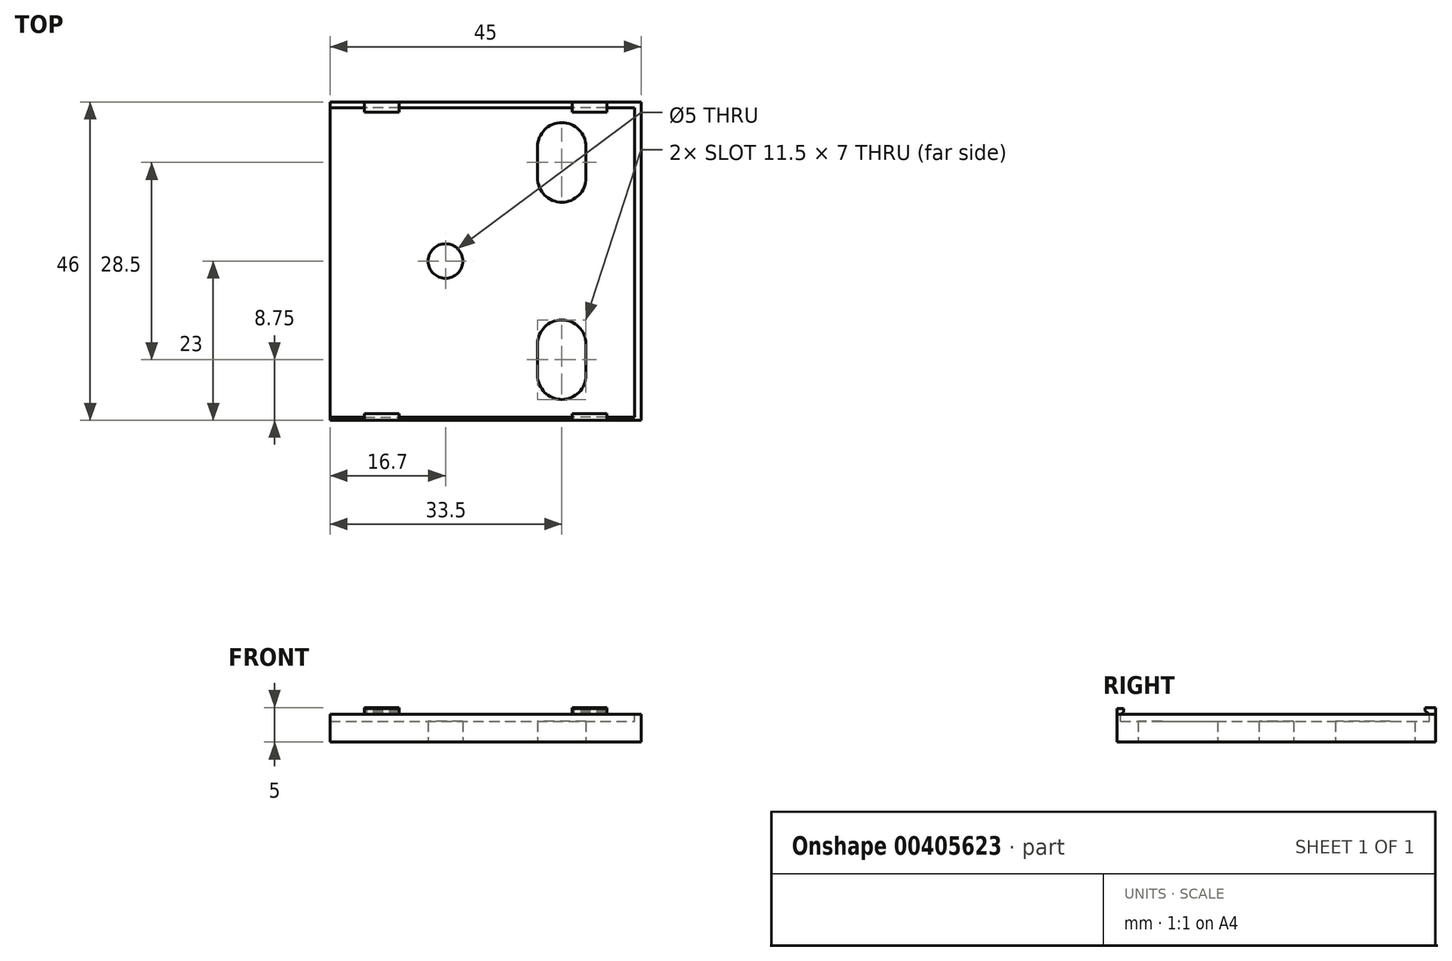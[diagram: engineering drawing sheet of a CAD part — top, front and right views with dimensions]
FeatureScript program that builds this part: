
annotation { "Feature Type Name" : "Feature", "Feature Type Description" : "" }
export const myFeature = defineFeature(function(context is Context, id is Id, definition is map)
    precondition{}
    {
        {
            var Q0;
            Q0=qCreatedBy(makeId("Top.planeOp"),FACE);
            var sketch = newSketch(context, id + "F0", { "sketchPlane" : qUnion([Q0])});
            skLineSegment(sketch, "E0.bottom", {"start": v(0, 0) * mm, "end": v(45, 0) * mm});
            skLineSegment(sketch, "E0.top", {"start": v(0, 46) * mm, "end": v(45, 46) * mm});
            skLineSegment(sketch, "E0.left", {"start": v(0, 0) * mm, "end": v(0, 46) * mm});
            skLineSegment(sketch, "E0.right", {"start": v(45, 0) * mm, "end": v(45, 46) * mm});
            skCircle(sketch, "E1", {"center": v(16.7, 23) * mm, "radius": 2.5 * mm});
            skPoint(sketch, "E1.centerSnap0", {"position": v(0, 23) * mm});
            skLineSegment(sketch, "E2.bottom", {"start": v(30, 39.5) * mm, "end": v(37, 39.5) * mm});
            skLineSegment(sketch, "E2.top", {"start": v(30, 35) * mm, "end": v(37, 35) * mm});
            skLineSegment(sketch, "E2.left", {"start": v(30, 39.5) * mm, "end": v(30, 35) * mm});
            skLineSegment(sketch, "E2.right", {"start": v(37, 39.5) * mm, "end": v(37, 35) * mm});
            skArc(sketch, "E3", {"start": v(37, 39.5) * mm, "mid": v(33.5, 43) * mm, "end": v(30, 39.5) * mm});
            skArc(sketch, "E4", {"start": v(30, 35) * mm, "mid": v(33.5, 31.5) * mm, "end": v(37, 35) * mm});
            skLineSegment(sketch, "E5", {"start": v(0, 23) * mm, "end": v(48.86, 23) * mm, "construction": true});
            skLineSegment(sketch, "E6.MirrorCS", {"start": v(30, 6.5) * mm, "end": v(30, 11) * mm});
            skLineSegment(sketch, "E7.MirrorCS", {"start": v(37, 6.5) * mm, "end": v(37, 11) * mm});
            skArc(sketch, "E8.MirrorCS", {"start": v(30, 11) * mm, "mid": v(33.5, 14.5) * mm, "end": v(37, 11) * mm});
            skArc(sketch, "E9.MirrorCS", {"start": v(37, 6.5) * mm, "mid": v(33.5, 3) * mm, "end": v(30, 6.5) * mm});
            skSolve(sketch);
        }
        {
            var Q0;
            Q0=makeQuery(id+"F0.imprint","IMPRINT",FACE,{"disambiguationData":[TD([[makeQuery(id+"F0.imprint","IMPRINT",EDGE,{"derivedFrom":sQuery(id+"F0.wireOp",EDGE,"E0.bottom")}),1.0]])]});
            extrude(context, id + "F1", {"entities" : qUnion([Q0]), "depth" : 4 * mm, "offsetDistance" : 25 * mm});
        }
        {
            var Q0;
            Q0=makeQuery(id+"F1.opExtrude","CAP_FACE",FACE,{"disambiguationData":[OSD([sQuery(id+"F0.wireOp",EDGE,"E0.bottom"),sQuery(id+"F0.wireOp",EDGE,"E0.top"),sQuery(id+"F0.wireOp",EDGE,"E0.left"),sQuery(id+"F0.wireOp",EDGE,"E0.right"),sQuery(id+"F0.wireOp",EDGE,"E1"),sQuery(id+"F0.wireOp",EDGE,"E2.left"),sQuery(id+"F0.wireOp",EDGE,"E2.right"),sQuery(id+"F0.wireOp",EDGE,"E3"),sQuery(id+"F0.wireOp",EDGE,"E4"),sQuery(id+"F0.wireOp",EDGE,"E6.MirrorCS"),sQuery(id+"F0.wireOp",EDGE,"E7.MirrorCS"),sQuery(id+"F0.wireOp",EDGE,"E8.MirrorCS"),sQuery(id+"F0.wireOp",EDGE,"E9.MirrorCS")])],"isStart":false});
            var sketch = newSketch(context, id + "F2", { "sketchPlane" : qUnion([Q0])});
            skLineSegment(sketch, "E10.bottom", {"start": v(0, 45.15) * mm, "end": v(44, 45.15) * mm});
            skLineSegment(sketch, "E10.top", {"start": v(0, 0.45) * mm, "end": v(44, 0.45) * mm});
            skLineSegment(sketch, "E10.left", {"start": v(0, 45.15) * mm, "end": v(0, 0.45) * mm});
            skLineSegment(sketch, "E10.right", {"start": v(44, 45.15) * mm, "end": v(44, 0.45) * mm});
            skSolve(sketch);
        }
        {
            var Q0;
            Q0=makeQuery(id+"F2.imprint","IMPRINT",FACE,{"disambiguationData":[TD([[makeQuery(id+"F2.imprint","IMPRINT",EDGE,{"derivedFrom":sQuery(id+"F2.wireOp",EDGE,"E10.bottom")}),-1.0]])]});
            extrude(context, id + "F3", {"entities" : qUnion([Q0]), "operationType" : NewBodyOperationType.REMOVE, "oppositeDirection" : true, "depth" : 1 * mm, "offsetDistance" : 25 * mm});
        }
        {
            var Q0;
            Q0=makeQuery(id+"F1.opExtrude","SWEPT_FACE",FACE,{"disambiguationData":[OSD([sQuery(id+"F0.wireOp",EDGE,"E0.left")])]});
            var sketch = newSketch(context, id + "F4", { "sketchPlane" : qUnion([Q0])});
            skLineSegment(sketch, "E11", {"start": v(-45.15, 4) * mm, "end": v(-46, 4) * mm});
            skLineSegment(sketch, "E12", {"start": v(-46, 4) * mm, "end": v(-46, 5) * mm});
            skLineSegment(sketch, "E13", {"start": v(-46, 5) * mm, "end": v(-44.5, 5) * mm});
            skLineSegment(sketch, "E14", {"start": v(-44.5, 5) * mm, "end": v(-44.5, 4.5) * mm});
            skLineSegment(sketch, "E15", {"start": v(-44.5, 4.5) * mm, "end": v(-45.15, 4) * mm});
            skLineSegment(sketch, "E16", {"start": v(-23, 0) * mm, "end": v(-23, 7.86) * mm, "construction": true});
            skLineSegment(sketch, "E17", {"start": v(-0.45, 4) * mm, "end": v(0, 4) * mm});
            skLineSegment(sketch, "E18", {"start": v(0, 4) * mm, "end": v(0, 4.83) * mm});
            skLineSegment(sketch, "E19", {"start": v(0, 4.83) * mm, "end": v(-0.95, 4.83) * mm});
            skLineSegment(sketch, "E20", {"start": v(-0.95, 4.83) * mm, "end": v(-0.95, 4.33) * mm});
            skLineSegment(sketch, "E21", {"start": v(-0.95, 4.33) * mm, "end": v(-0.45, 4) * mm});
            skSolve(sketch);
        }
        {
            var Q0;
            Q0=makeQuery(id+"F4.imprint","IMPRINT",FACE,{"disambiguationData":[TD([[makeQuery(id+"F4.imprint","IMPRINT",EDGE,{"derivedFrom":sQuery(id+"F4.wireOp",EDGE,"E11")}),-1.0]])]});
            var Q1;
            Q1=makeQuery(id+"F4.imprint","IMPRINT",FACE,{"disambiguationData":[TD([[makeQuery(id+"F4.imprint","IMPRINT",EDGE,{"derivedFrom":sQuery(id+"F4.wireOp",EDGE,"a72cb571-9186-48ee-92ca-6ca3befd67920.MirrorCS")}),1.0]])]});
            extrude(context, id + "F5", {"entities" : qUnion([Q0, Q1]), "oppositeDirection" : true, "depth" : 5 * mm, "offsetDistance" : 25 * mm});
        }
        {
            var Q0;
            Q0=makeQuery(id+"F4.imprint","IMPRINT",FACE,{"disambiguationData":[TD([[makeQuery(id+"F4.imprint","IMPRINT",EDGE,{"derivedFrom":sQuery(id+"F4.wireOp",EDGE,"E17")}),-1.0]])]});
            extrude(context, id + "F6", {"entities" : qUnion([Q0]), "oppositeDirection" : true, "depth" : 5 * mm, "offsetDistance" : 25 * mm});
        }
        {
            var Q0;
            Q0=makeQuery(id+"F6.opExtrude","SWEPT_BODY",BODY,{"disambiguationData":[OSD([sQuery(id+"F4.wireOp",EDGE,"E17"),sQuery(id+"F4.wireOp",EDGE,"E18"),sQuery(id+"F4.wireOp",EDGE,"E19"),sQuery(id+"F4.wireOp",EDGE,"E20"),sQuery(id+"F4.wireOp",EDGE,"E21")])]});
            transform(context, id + "F7", {"entities" : qUnion([Q0]), "transformType" : TransformType.TRANSLATION_3D, "dx" : 40 * mm, "dy" : 0 * mm, "dz" : 0 * mm, "makeCopy" : true});
        }
        {
            var Q0;
            Q0=makeQuery(id+"F5.opExtrude","SWEPT_BODY",BODY,{"disambiguationData":[OSD([sQuery(id+"F4.wireOp",EDGE,"E11"),sQuery(id+"F4.wireOp",EDGE,"E12"),sQuery(id+"F4.wireOp",EDGE,"E13"),sQuery(id+"F4.wireOp",EDGE,"E14"),sQuery(id+"F4.wireOp",EDGE,"E15")])]});
            transform(context, id + "F8", {"entities" : qUnion([Q0]), "transformType" : TransformType.TRANSLATION_3D, "dx" : 40 * mm, "dy" : 0 * mm, "dz" : 0 * mm, "makeCopy" : true});
        }
        {
            var Q0;
            Q0=makeQuery(id+"F5.opExtrude","SWEPT_BODY",BODY,{"disambiguationData":[OSD([sQuery(id+"F4.wireOp",EDGE,"E11"),sQuery(id+"F4.wireOp",EDGE,"E12"),sQuery(id+"F4.wireOp",EDGE,"E13"),sQuery(id+"F4.wireOp",EDGE,"E14"),sQuery(id+"F4.wireOp",EDGE,"E15")])]});
            var Q1;
            Q1=makeQuery(id+"F6.opExtrude","SWEPT_BODY",BODY,{"disambiguationData":[OSD([sQuery(id+"F4.wireOp",EDGE,"E17"),sQuery(id+"F4.wireOp",EDGE,"E18"),sQuery(id+"F4.wireOp",EDGE,"E19"),sQuery(id+"F4.wireOp",EDGE,"E20"),sQuery(id+"F4.wireOp",EDGE,"E21")])]});
            transform(context, id + "F9", {"entities" : qUnion([Q0, Q1]), "transformType" : TransformType.TRANSLATION_3D, "dx" : 5 * mm, "dy" : 0 * mm, "dz" : 0 * mm, "makeCopy" : false});
        }
        {
            var Q0;
            Q0=makeQuery(id+"F7.opPattern","COPY",BODY,{"derivedFrom":makeQuery(id+"F6.opExtrude","SWEPT_BODY",BODY,{"disambiguationData":[OSD([sQuery(id+"F4.wireOp",EDGE,"E17"),sQuery(id+"F4.wireOp",EDGE,"E18"),sQuery(id+"F4.wireOp",EDGE,"E19"),sQuery(id+"F4.wireOp",EDGE,"E20"),sQuery(id+"F4.wireOp",EDGE,"E21")])]}),"instanceName":"1"});
            var Q1;
            Q1=makeQuery(id+"F8.opPattern","COPY",BODY,{"derivedFrom":makeQuery(id+"F5.opExtrude","SWEPT_BODY",BODY,{"disambiguationData":[OSD([sQuery(id+"F4.wireOp",EDGE,"E11"),sQuery(id+"F4.wireOp",EDGE,"E12"),sQuery(id+"F4.wireOp",EDGE,"E13"),sQuery(id+"F4.wireOp",EDGE,"E14"),sQuery(id+"F4.wireOp",EDGE,"E15")])]}),"instanceName":"1"});
            transform(context, id + "F10", {"entities" : qUnion([Q0, Q1]), "transformType" : TransformType.TRANSLATION_3D, "dx" : -5 * mm, "dy" : 0 * mm, "dz" : 0 * mm, "makeCopy" : false});
        }
    });
